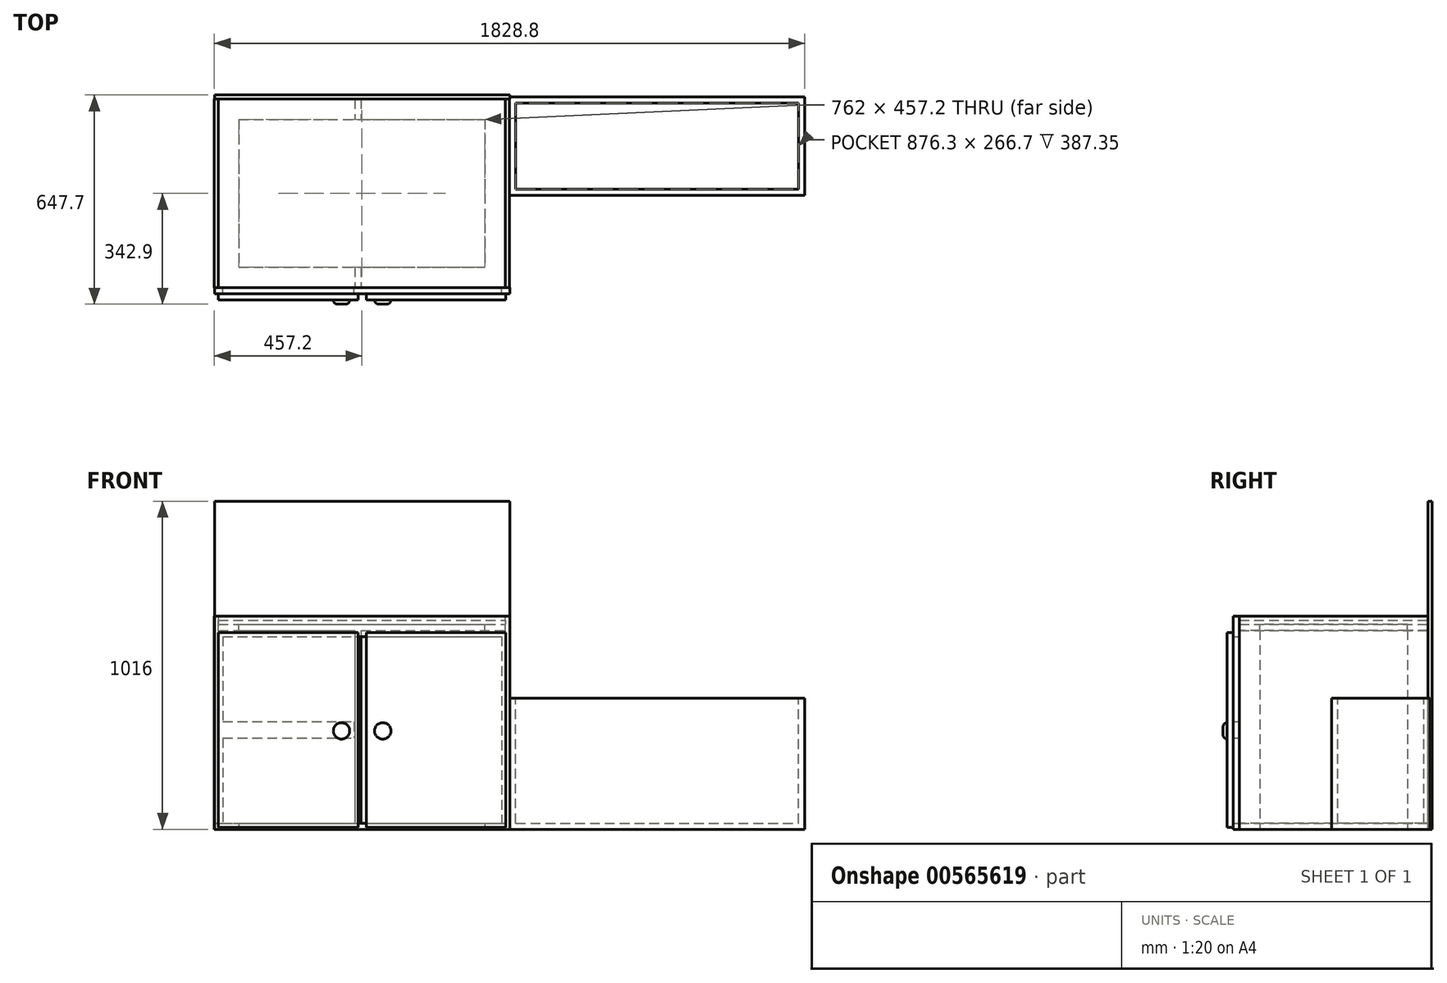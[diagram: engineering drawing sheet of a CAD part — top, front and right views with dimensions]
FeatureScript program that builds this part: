
annotation { "Feature Type Name" : "Feature", "Feature Type Description" : "" }
export const myFeature = defineFeature(function(context is Context, id is Id, definition is map)
    precondition{}
    {
        {
            var Q0;
            Q0=qCreatedBy(makeId("Top.planeOp"),FACE);
            var sketch = newSketch(context, id + "F0", { "sketchPlane" : qUnion([Q0])});
            skLineSegment(sketch, "E0.bottom", {"start": v(0, 0) * mm, "end": v(889, 0) * mm});
            skLineSegment(sketch, "E0.top", {"start": v(0, 584.2) * mm, "end": v(889, 584.2) * mm});
            skLineSegment(sketch, "E0.left", {"start": v(0, 0) * mm, "end": v(0, 584.2) * mm});
            skLineSegment(sketch, "E0.right", {"start": v(889, 0) * mm, "end": v(889, 584.2) * mm});
            skLineSegment(sketch, "E1", {"start": v(0, 520.7) * mm, "end": v(889, 520.7) * mm});
            skLineSegment(sketch, "E2", {"start": v(0, 63.5) * mm, "end": v(889, 63.5) * mm});
            skLineSegment(sketch, "E3", {"start": v(63.5, 520.7) * mm, "end": v(63.5, 63.5) * mm});
            skLineSegment(sketch, "E4", {"start": v(825.5, 520.7) * mm, "end": v(825.5, 63.5) * mm});
            skSolve(sketch);
        }
        {
            var Q0;
            Q0 = qSketchRegion(id + "F0", true);
            extrude(context, id + "F1", {"entities" : qUnion([Q0]), "depth" : 19.05 * mm, "offsetDistance" : 25.4 * mm});
        }
        {
            var Q0;
            Q0=makeQuery(id+"F1.opExtrude","SWEPT_FACE",FACE,{"disambiguationData":[OSD([sQuery(id+"F0.wireOp",EDGE,"E0.right")])]});
            var sketch = newSketch(context, id + "F2", { "sketchPlane" : qUnion([Q0])});
            skLineSegment(sketch, "E5.bottom", {"start": v(0, 0) * mm, "end": v(584.2, 0) * mm});
            skLineSegment(sketch, "E5.top", {"start": v(0, 660.4) * mm, "end": v(584.2, 660.4) * mm});
            skLineSegment(sketch, "E5.left", {"start": v(0, 0) * mm, "end": v(0, 660.4) * mm});
            skLineSegment(sketch, "E5.right", {"start": v(584.2, 0) * mm, "end": v(584.2, 660.4) * mm});
            skSolve(sketch);
        }
        {
            var Q0;
            {var subQ4=sQuery(id+"F2.wireOp",EDGE,"E5.top");Q0=makeQuery(id+"F2.imprint","IMPRINT",FACE,{"disambiguationData":[TD([[makeQuery(id+"F2.imprint","IMPRINT",EDGE,{"derivedFrom":subQ4}),-1.0]])]});}
            var Q1;
            {var subQ3=sQuery(id+"F0.wireOp",EDGE,"E0.right");var subQ5=makeQuery(id+"F1.opExtrude","CAP_EDGE",EDGE,{"disambiguationData":[OSD([subQ3])],"isStart":false});Q1=makeQuery(id+"F2.imprint","IMPRINT",FACE,{"disambiguationData":[TD([[makeQuery(id+"F2.imprint","IMPRINT",EDGE,{"derivedFrom":subQ5}),-1.0]])]});}
            extrude(context, id + "F3", {"entities" : qUnion([Q0, Q1]), "depth" : 12.7 * mm, "offsetDistance" : 25.4 * mm});
        }
        {
            var Q0;
            Q0=makeQuery(id+"F1.opExtrude","SWEPT_FACE",FACE,{"disambiguationData":[OSD([sQuery(id+"F0.wireOp",EDGE,"E0.left")])]});
            var sketch = newSketch(context, id + "F4", { "sketchPlane" : qUnion([Q0])});
            skLineSegment(sketch, "E6.bottom", {"start": v(-6.12, -0.38) * mm, "end": v(-583.97, -0.38) * mm});
            skLineSegment(sketch, "E6.top", {"start": v(0, 660.02) * mm, "end": v(-583.97, 660.02) * mm});
            skLineSegment(sketch, "E6.left", {"start": v(0, 0) * mm, "end": v(0, 660.02) * mm});
            skLineSegment(sketch, "E6.right", {"start": v(-583.97, -0.38) * mm, "end": v(-583.97, 660.02) * mm});
            skSolve(sketch);
        }
        {
            var Q0;
            {var subQ3=sQuery(id+"F0.wireOp",EDGE,"E0.left");var subQ5=makeQuery(id+"F1.opExtrude","CAP_EDGE",EDGE,{"disambiguationData":[OSD([subQ3])],"isStart":false});Q0=makeQuery(id+"F4.imprint","IMPRINT",FACE,{"disambiguationData":[TD([[makeQuery(id+"F4.imprint","IMPRINT",EDGE,{"derivedFrom":subQ5}),1.0]])]});}
            var Q1;
            {var subQ3=sQuery(id+"F4.wireOp",EDGE,"E6.top");Q1=makeQuery(id+"F4.imprint","IMPRINT",FACE,{"disambiguationData":[TD([[makeQuery(id+"F4.imprint","IMPRINT",EDGE,{"derivedFrom":subQ3}),1.0]])]});}
            extrude(context, id + "F5", {"entities" : qUnion([Q0, Q1]), "depth" : 12.7 * mm, "offsetDistance" : 25.4 * mm});
        }
        {
            var Q0;
            Q0=makeQuery(id+"F1.opExtrude","SWEPT_FACE",FACE,{"disambiguationData":[OSD([sQuery(id+"F0.wireOp",EDGE,"E0.top")])]});
            var sketch = newSketch(context, id + "F6", { "sketchPlane" : qUnion([Q0])});
            skLineSegment(sketch, "E7.bottom", {"start": v(-902.12, 0) * mm, "end": v(12.28, 0) * mm});
            skLineSegment(sketch, "E7.top", {"start": v(-902.12, 1016) * mm, "end": v(12.28, 1016) * mm});
            skLineSegment(sketch, "E7.left", {"start": v(-902.12, 0) * mm, "end": v(-902.12, 1016) * mm});
            skLineSegment(sketch, "E7.right", {"start": v(12.28, 0) * mm, "end": v(12.28, 1016) * mm});
            skSolve(sketch);
        }
        {
            var Q0;
            Q0 = qSketchRegion(id + "F6", true);
            extrude(context, id + "F7", {"entities" : qUnion([Q0]), "depth" : 12.7 * mm, "offsetDistance" : 25.4 * mm});
        }
        {
            var Q0;
            Q0=makeQuery(id+"F1.opExtrude","SWEPT_FACE",FACE,{"disambiguationData":[OSD([sQuery(id+"F0.wireOp",EDGE,"E0.bottom")])]});
            var sketch = newSketch(context, id + "F8", { "sketchPlane" : qUnion([Q0])});
            skLineSegment(sketch, "E8.bottom", {"start": v(-11.93, 0) * mm, "end": v(902.47, 0) * mm});
            skLineSegment(sketch, "E8.top", {"start": v(-11.93, 660.4) * mm, "end": v(902.47, 660.4) * mm});
            skLineSegment(sketch, "E8.left", {"start": v(-11.93, 0) * mm, "end": v(-11.93, 660.4) * mm});
            skLineSegment(sketch, "E8.right", {"start": v(902.47, 0) * mm, "end": v(902.47, 660.4) * mm});
            skLineSegment(sketch, "E9", {"start": v(-11.93, 19.05) * mm, "end": v(902.47, 19.05) * mm});
            skLineSegment(sketch, "E10", {"start": v(-11.93, 596.9) * mm, "end": v(902.47, 596.9) * mm});
            skLineSegment(sketch, "E11", {"start": v(13.47, 596.9) * mm, "end": v(13.47, 19.05) * mm});
            skLineSegment(sketch, "E12", {"start": v(877.07, 596.9) * mm, "end": v(877.07, 19.05) * mm});
            skLineSegment(sketch, "E13.bottom", {"start": v(419.87, 596.9) * mm, "end": v(470.67, 596.9) * mm});
            skLineSegment(sketch, "E13.top", {"start": v(419.87, 19.05) * mm, "end": v(470.67, 19.05) * mm});
            skLineSegment(sketch, "E13.left", {"start": v(419.87, 596.9) * mm, "end": v(419.87, 19.05) * mm});
            skLineSegment(sketch, "E13.right", {"start": v(470.67, 596.9) * mm, "end": v(470.67, 19.05) * mm});
            skLineSegment(sketch, "E14.bottom", {"start": v(13.47, 333.38) * mm, "end": v(419.87, 333.38) * mm});
            skLineSegment(sketch, "E14.top", {"start": v(13.47, 282.57) * mm, "end": v(419.87, 282.58) * mm});
            skLineSegment(sketch, "E14.left", {"start": v(13.47, 333.38) * mm, "end": v(13.47, 282.57) * mm});
            skLineSegment(sketch, "E14.right", {"start": v(419.87, 333.38) * mm, "end": v(419.87, 282.58) * mm});
            skSolve(sketch);
        }
        {
            var Q0;
            Q0 = qSketchRegion(id + "F8", true);
            var Q1;
            Q1=makeQuery(id+"F8.imprint","IMPRINT",FACE,{"disambiguationData":[TD([[makeQuery(id+"F8.imprint","IMPRINT",EDGE,{"derivedFrom":sQuery(id+"F8.wireOp",EDGE,"E13.bottom")}),-1.0]])]});
            var Q2;
            Q2=makeQuery(id+"F8.imprint","IMPRINT",FACE,{"disambiguationData":[TD([[makeQuery(id+"F8.imprint","IMPRINT",EDGE,{"derivedFrom":sQuery(id+"F8.wireOp",EDGE,"E14.bottom")}),-1.0]])]});
            var Q3;
            Q3=makeQuery(id+"F8.imprint","IMPRINT",FACE,{"disambiguationData":[TD([[makeQuery(id+"F8.imprint","IMPRINT",EDGE,{"derivedFrom":sQuery(id+"F8.wireOp",EDGE,"dXFfynaj-yA0K-9rLG-yDad-npvW6kytxtA9.bottom")}),-1.0]])]});
            extrude(context, id + "F9", {"entities" : qUnion([Q0, Q1, Q2, Q3]), "depth" : 19.05 * mm, "offsetDistance" : 25.4 * mm});
        }
        {
            var Q0;
            Q0=makeQuery(id+"F9.opExtrude","CAP_FACE",FACE,{"disambiguationData":[OSD([sQuery(id+"F8.wireOp",EDGE,"E8.bottom"),sQuery(id+"F8.wireOp",EDGE,"E8.top"),sQuery(id+"F8.wireOp",EDGE,"E8.left"),sQuery(id+"F8.wireOp",EDGE,"E8.right"),sQuery(id+"F8.wireOp",EDGE,"E9"),sQuery(id+"F8.wireOp",EDGE,"E10"),sQuery(id+"F8.wireOp",EDGE,"E11"),sQuery(id+"F8.wireOp",EDGE,"E12"),sQuery(id+"F8.wireOp",EDGE,"E13.left"),sQuery(id+"F8.wireOp",EDGE,"E13.right"),sQuery(id+"F8.wireOp",EDGE,"E14.bottom"),sQuery(id+"F8.wireOp",EDGE,"E14.top"),sQuery(id+"F8.wireOp",EDGE,"dXFfynaj-yA0K-9rLG-yDad-npvW6kytxtA9.bottom"),sQuery(id+"F8.wireOp",EDGE,"dXFfynaj-yA0K-9rLG-yDad-npvW6kytxtA9.top")])],"isStart":false});
            var sketch = newSketch(context, id + "F10", { "sketchPlane" : qUnion([Q0])});
            skLineSegment(sketch, "E15.bottom", {"start": v(457.97, 609.6) * mm, "end": v(889.77, 609.6) * mm});
            skLineSegment(sketch, "E15.top", {"start": v(457.97, 6.35) * mm, "end": v(889.77, 6.35) * mm});
            skLineSegment(sketch, "E15.left", {"start": v(457.97, 609.6) * mm, "end": v(457.97, 6.35) * mm});
            skLineSegment(sketch, "E15.right", {"start": v(889.77, 609.6) * mm, "end": v(889.77, 6.35) * mm});
            skLineSegment(sketch, "E16.bottom", {"start": v(432.57, 609.6) * mm, "end": v(0, 609.6) * mm});
            skLineSegment(sketch, "E16.top", {"start": v(432.57, 6.35) * mm, "end": v(0, 6.35) * mm});
            skLineSegment(sketch, "E16.left", {"start": v(432.57, 609.6) * mm, "end": v(432.57, 6.35) * mm});
            skLineSegment(sketch, "E16.right", {"start": v(0, 609.6) * mm, "end": v(0, 6.35) * mm});
            skSolve(sketch);
        }
        {
            var Q0;
            Q0=makeQuery(id+"F10.imprint","IMPRINT",FACE,{"disambiguationData":[TD([[makeQuery(id+"F10.imprint","IMPRINT",EDGE,{"derivedFrom":sQuery(id+"F10.wireOp",EDGE,"E15.bottom")}),-1.0]])]});
            var Q1;
            {var subQ0=sQuery(id+"F8.wireOp",EDGE,"E12");Q1=makeQuery(id+"F10.imprint","IMPRINT",FACE,{"disambiguationData":[TD([[makeQuery(id+"F10.imprint","IMPRINT",EDGE,{"derivedFrom":makeQuery(id+"F9.opExtrude","CAP_EDGE",EDGE,{"disambiguationData":[OSD([subQ0])],"isStart":false})}),-1.0]])]});}
            var Q2;
            Q2=makeQuery(id+"F10.imprint","IMPRINT",FACE,{"disambiguationData":[TD([[makeQuery(id+"F10.imprint","IMPRINT",EDGE,{"derivedFrom":sQuery(id+"F10.wireOp",EDGE,"E16.bottom")}),1.0]])]});
            var Q3;
            {var subQ5=sQuery(id+"F8.wireOp",EDGE,"E14.bottom");Q3=makeQuery(id+"F10.imprint","IMPRINT",FACE,{"disambiguationData":[TD([[makeQuery(id+"F10.imprint","IMPRINT",EDGE,{"derivedFrom":makeQuery(id+"F9.opExtrude","CAP_EDGE",EDGE,{"disambiguationData":[OSD([subQ5])],"isStart":false})}),1.0]])]});}
            var Q4;
            {var subQ5=sQuery(id+"F8.wireOp",EDGE,"E14.top");Q4=makeQuery(id+"F10.imprint","IMPRINT",FACE,{"disambiguationData":[TD([[makeQuery(id+"F10.imprint","IMPRINT",EDGE,{"derivedFrom":makeQuery(id+"F9.opExtrude","CAP_EDGE",EDGE,{"disambiguationData":[OSD([subQ5])],"isStart":false})}),-1.0]])]});}
            extrude(context, id + "F11", {"entities" : qUnion([Q0, Q1, Q2, Q3, Q4]), "operationType" : NewBodyOperationType.ADD, "depth" : 19.05 * mm, "offsetDistance" : 25.4 * mm});
        }
        {
            var Q0;
            Q0=makeQuery(id+"F11.opExtrude","CAP_FACE",FACE,{"disambiguationData":[OSD([sQuery(id+"F10.wireOp",EDGE,"E15.bottom"),sQuery(id+"F10.wireOp",EDGE,"E15.top"),sQuery(id+"F10.wireOp",EDGE,"E15.left"),sQuery(id+"F10.wireOp",EDGE,"E15.right")])],"isStart":false});
            var sketch = newSketch(context, id + "F12", { "sketchPlane" : qUnion([Q0])});
            skCircle(sketch, "E17", {"center": v(508.77, 304.8) * mm, "radius": 25.4 * mm});
            skCircle(sketch, "E18", {"center": v(381, 304.8) * mm, "radius": 25.4 * mm});
            skSolve(sketch);
        }
        {
            var Q0;
            Q0 = qSketchRegion(id + "F12", true);
            extrude(context, id + "F13", {"entities" : qUnion([Q0]), "operationType" : NewBodyOperationType.ADD, "depth" : 12.7 * mm, "offsetDistance" : 25.4 * mm});
        }
        {
            var Q0;
            Q0=makeQuery(id+"F13.opExtrude","CAP_FACE",FACE,{"disambiguationData":[OSD([sQuery(id+"F12.wireOp",EDGE,"E17")])],"isStart":false});
            var Q1;
            Q1=makeQuery(id+"F13.opExtrude","CAP_FACE",FACE,{"disambiguationData":[OSD([sQuery(id+"F12.wireOp",EDGE,"E18")])],"isStart":false});
            fillet(context, id + "F14", {"entities" : qUnion([Q0, Q1]), "radius" : 12.7 * mm, "tangentPropagation" : true, "allowEdgeOverflow" : false});
        }
        {
            var Q0;
            Q0=makeQuery(id+"F3.opExtrude","CAP_FACE",FACE,{"disambiguationData":[OSD([sQuery(id+"F2.wireOp",EDGE,"E5.bottom"),sQuery(id+"F2.wireOp",EDGE,"E5.top"),sQuery(id+"F2.wireOp",EDGE,"E5.left"),sQuery(id+"F2.wireOp",EDGE,"E5.right")])],"isStart":false});
            var sketch = newSketch(context, id + "F15", { "sketchPlane" : qUnion([Q0])});
            skLineSegment(sketch, "E19.bottom", {"start": v(590.4, 406.4) * mm, "end": v(285.6, 406.4) * mm});
            skLineSegment(sketch, "E19.top", {"start": v(590.4, 0) * mm, "end": v(285.6, 0) * mm});
            skLineSegment(sketch, "E19.left", {"start": v(590.4, 406.4) * mm, "end": v(590.4, 0) * mm});
            skLineSegment(sketch, "E19.right", {"start": v(285.6, 406.4) * mm, "end": v(285.6, 0) * mm});
            skSolve(sketch);
        }
        {
            var Q0;
            Q0 = qSketchRegion(id + "F15", true);
            extrude(context, id + "F16", {"entities" : qUnion([Q0]), "depth" : 914.4 * mm, "offsetDistance" : 25.4 * mm});
        }
        {
            var Q0;
            Q0=makeQuery(id+"F16.opExtrude","SWEPT_FACE",FACE,{"disambiguationData":[OSD([sQuery(id+"F15.wireOp",EDGE,"E19.bottom")])]});
            var sketch = newSketch(context, id + "F17", { "sketchPlane" : qUnion([Q0])});
            skLineSegment(sketch, "E20.bottom", {"start": v(920.75, 571.36) * mm, "end": v(1797.05, 571.36) * mm});
            skLineSegment(sketch, "E20.top", {"start": v(920.75, 304.66) * mm, "end": v(1797.05, 304.66) * mm});
            skLineSegment(sketch, "E20.left", {"start": v(920.75, 571.36) * mm, "end": v(920.75, 304.66) * mm});
            skLineSegment(sketch, "E20.right", {"start": v(1797.05, 571.36) * mm, "end": v(1797.05, 304.66) * mm});
            skSolve(sketch);
        }
        {
            var Q0;
            Q0=qCreatedBy(makeId("Top.planeOp"),FACE);
            cPlane(context, id + "F18", {"entities" : qUnion([Q0]), "cplaneType" : CPlaneType.OFFSET, "offset" : 635 * mm, "width" : 152.4 * mm, "height" : 152.4 * mm});
        }
        {
            var Q0;
            Q0 = qSketchRegion(id + "F17", true);
            var Q1;
            Q1=makeQuery(id+"F16.opExtrude","SWEPT_FACE",FACE,{"disambiguationData":[OSD([sQuery(id+"F15.wireOp",EDGE,"E19.top")])]});
            extrude(context, id + "F19", {"entities" : qUnion([Q0]), "operationType" : NewBodyOperationType.REMOVE, "endBound" : BoundingType.UP_TO_SURFACE, "oppositeDirection" : true, "depth" : 25.4 * mm, "endBoundEntityFace" : qUnion([Q1]), "hasOffset" : true, "offsetDistance" : 19.05 * mm});
        }
        {
            var Q0;
            Q0=qCreatedBy(id+"F18.planeOp",FACE);
            var sketch = newSketch(context, id + "F20", { "sketchPlane" : qUnion([Q0])});
            skLineSegment(sketch, "E21.bottom", {"start": v(0, 0) * mm, "end": v(889, 0) * mm});
            skLineSegment(sketch, "E21.top", {"start": v(0, 584.2) * mm, "end": v(889, 584.2) * mm});
            skLineSegment(sketch, "E21.left", {"start": v(0, 0) * mm, "end": v(0, 584.2) * mm});
            skLineSegment(sketch, "E21.right", {"start": v(889, 0) * mm, "end": v(889, 584.2) * mm});
            skLineSegment(sketch, "E22", {"start": v(0, 520.7) * mm, "end": v(889, 520.7) * mm});
            skLineSegment(sketch, "E23", {"start": v(0, 63.5) * mm, "end": v(889, 63.5) * mm});
            skLineSegment(sketch, "E24", {"start": v(63.5, 520.7) * mm, "end": v(63.5, 63.5) * mm});
            skLineSegment(sketch, "E25", {"start": v(825.5, 520.7) * mm, "end": v(825.5, 63.5) * mm});
            skSolve(sketch);
        }
        {
            var Q0;
            Q0 = qSketchRegion(id + "F20", true);
            extrude(context, id + "F21", {"entities" : qUnion([Q0]), "oppositeDirection" : true, "depth" : 19.05 * mm, "offsetDistance" : 25.4 * mm});
        }
        {
            var Q0;
            Q0=makeQuery(id+"F1.opExtrude","CAP_FACE",FACE,{"disambiguationData":[OSD([sQuery(id+"F0.wireOp",EDGE,"E0.bottom"),sQuery(id+"F0.wireOp",EDGE,"E0.top"),sQuery(id+"F0.wireOp",EDGE,"E0.left"),sQuery(id+"F0.wireOp",EDGE,"E0.right"),sQuery(id+"F0.wireOp",EDGE,"E1"),sQuery(id+"F0.wireOp",EDGE,"E2"),sQuery(id+"F0.wireOp",EDGE,"E3"),sQuery(id+"F0.wireOp",EDGE,"E4")])],"isStart":false});
            var sketch = newSketch(context, id + "F22", { "sketchPlane" : qUnion([Q0])});
            skLineSegment(sketch, "E26.bottom", {"start": v(422.28, 63.5) * mm, "end": v(441.33, 63.5) * mm});
            skLineSegment(sketch, "E26.top", {"start": v(422.28, 0) * mm, "end": v(441.33, 0) * mm});
            skLineSegment(sketch, "E26.left", {"start": v(422.28, 63.5) * mm, "end": v(422.28, 0) * mm});
            skLineSegment(sketch, "E26.right", {"start": v(441.33, 63.5) * mm, "end": v(441.33, 0) * mm});
            skLineSegment(sketch, "E27.bottom", {"start": v(422.27, 584.2) * mm, "end": v(441.33, 584.2) * mm});
            skLineSegment(sketch, "E27.top", {"start": v(422.27, 520.7) * mm, "end": v(441.33, 520.7) * mm});
            skLineSegment(sketch, "E27.left", {"start": v(422.27, 584.2) * mm, "end": v(422.27, 520.7) * mm});
            skLineSegment(sketch, "E27.right", {"start": v(441.33, 584.2) * mm, "end": v(441.33, 520.7) * mm});
            skSolve(sketch);
        }
        {
            var Q0;
            Q0 = qSketchRegion(id + "F22", true);
            var Q1;
            Q1=makeQuery(id+"F21.opExtrude","CAP_FACE",FACE,{"disambiguationData":[OSD([sQuery(id+"F20.wireOp",EDGE,"E21.bottom"),sQuery(id+"F20.wireOp",EDGE,"E21.top"),sQuery(id+"F20.wireOp",EDGE,"E21.left"),sQuery(id+"F20.wireOp",EDGE,"E21.right"),sQuery(id+"F20.wireOp",EDGE,"E22"),sQuery(id+"F20.wireOp",EDGE,"E23"),sQuery(id+"F20.wireOp",EDGE,"E24"),sQuery(id+"F20.wireOp",EDGE,"E25")])],"isStart":false});
            extrude(context, id + "F23", {"entities" : qUnion([Q0]), "operationType" : NewBodyOperationType.ADD, "endBound" : BoundingType.UP_TO_SURFACE, "depth" : 609.6 * mm, "endBoundEntityFace" : qUnion([Q1]), "offsetDistance" : 25.4 * mm});
        }
        {
            var Q0;
            Q0=makeQuery(id+"F21.opExtrude","CAP_FACE",FACE,{"disambiguationData":[OSD([sQuery(id+"F20.wireOp",EDGE,"E21.bottom"),sQuery(id+"F20.wireOp",EDGE,"E21.top"),sQuery(id+"F20.wireOp",EDGE,"E21.left"),sQuery(id+"F20.wireOp",EDGE,"E21.right"),sQuery(id+"F20.wireOp",EDGE,"E22"),sQuery(id+"F20.wireOp",EDGE,"E23"),sQuery(id+"F20.wireOp",EDGE,"E24"),sQuery(id+"F20.wireOp",EDGE,"E25")])],"isStart":true});
            var sketch = newSketch(context, id + "F24", { "sketchPlane" : qUnion([Q0])});
            skLineSegment(sketch, "E28.bottom", {"start": v(0, 584.2) * mm, "end": v(889, 584.2) * mm});
            skLineSegment(sketch, "E28.top", {"start": v(0, 0) * mm, "end": v(889, 0) * mm});
            skLineSegment(sketch, "E28.left", {"start": v(0, 584.2) * mm, "end": v(0, 0) * mm});
            skLineSegment(sketch, "E28.right", {"start": v(889, 584.2) * mm, "end": v(889, 0) * mm});
            skSolve(sketch);
        }
        {
            var Q0;
            Q0 = qSketchRegion(id + "F24", true);
            extrude(context, id + "F25", {"entities" : qUnion([Q0]), "depth" : 12.7 * mm, "offsetDistance" : 25.4 * mm});
        }
    });
